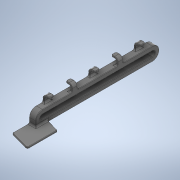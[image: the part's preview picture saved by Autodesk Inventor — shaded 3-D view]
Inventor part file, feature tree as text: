
AUTODESK INVENTOR PART (.ipt)
format: ipt  version: 2020 (Build 240168000, 168)  size: 502,272 bytes
history: native  units: mm
features: fillet x5, extrude x4, sketch x4, projected_geometry x3, pattern_linear x1
ambient origin geometry x8: Origin, YZ Plane, XZ Plane, XY Plane, X Axis, Y Axis, Z Axis, Center Point
bodies: Solid1 (feature_tree)
feature tree (17):
  extrude  "Extrusion1"  Depth=65.0mm
  extrude  "Extrusion2"  Depth=4.0mm TaperAngle=0.0deg
  extrude  "Extrusion3"  Depth=10.0mm
  extrude  "Extrusion4"  Depth=8.0mm
  pattern_linear  "Rectangular Pattern1"  Spacing1=1.0mm  [1 undecoded]
  fillet  "Fillet4"  Radius=1.0mm
  fillet  "Fillet5"  Radius=0.25mm
  fillet  "Fillet6"  Radius=3.0mm
  fillet  "Fillet1"  Radius=1.0mm
  fillet  "Fillet2"  Radius=13.5mm
  sketch  "Sketch1"  dims[d0=8.0mm d1=65.0mm]
  sketch  "Sketch2"  dims[d2=3.2mm d3=4.0mm d4=0.0mm]
  sketch  "Sketch4"  dims[d5=18.0mm d6=10.0mm]
  projected_geometry  "Projected Loop2"
  sketch  "Sketch5"  dims[d7=105.0deg d9=8.0mm d10=1.0mm d11=0.0mm d12=1.0mm d22=0.25mm d25=3.0mm d26=1.0mm d27=13.5mm d28=13.5mm d29=13.5mm d30=13.5mm d31=4.0mm d32=0.0mm d33=13.5mm d34=1.0mm d35=0.0mm d36=50.0mm d38=13.5mm d39=1.0mm d40=2.0mm d41=1.0mm]
  projected_geometry  "Projected Loop3"
  projected_geometry  "Projected Loop4"
note: 1 required parameter value undecoded (feature->parameter linkage not recoverable at this tier; creation-order binding heuristic only, values carry confidence <= 0.55)
